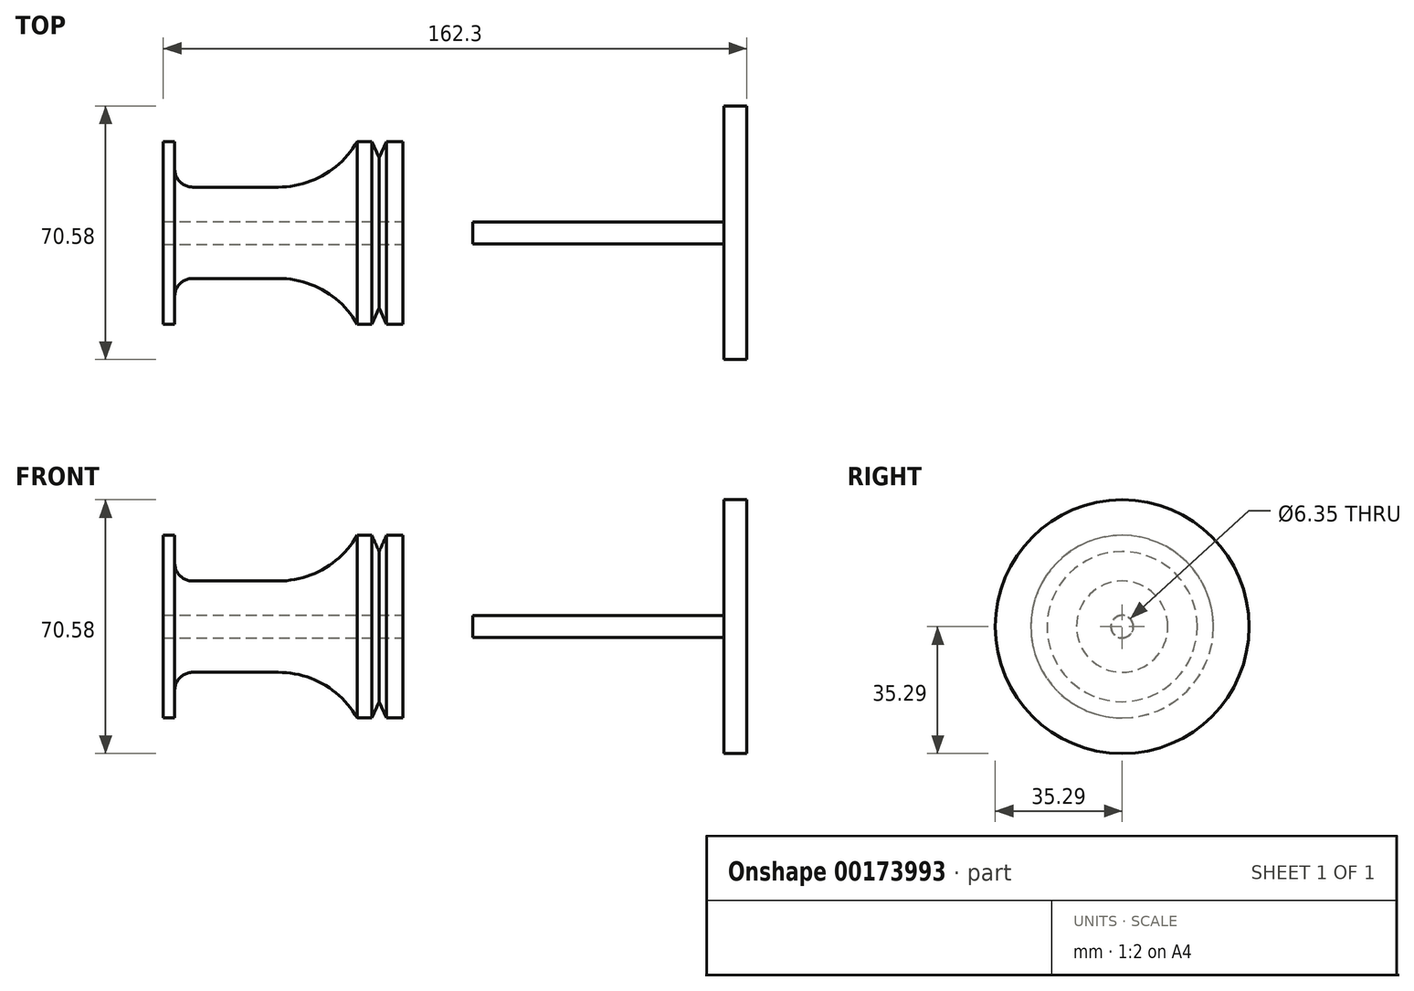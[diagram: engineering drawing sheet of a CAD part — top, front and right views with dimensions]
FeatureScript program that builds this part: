
annotation { "Feature Type Name" : "Feature", "Feature Type Description" : "" }
export const myFeature = defineFeature(function(context is Context, id is Id, definition is map)
    precondition{}
    {
        {
            var Q0;
            Q0=qCreatedBy(makeId("Front.planeOp"),FACE);
            var sketch = newSketch(context, id + "F0", { "sketchPlane" : qUnion([Q0])});
            skLineSegment(sketch, "E0", {"start": v(-70.82, 0) * mm, "end": v(-70.82, 25.4) * mm});
            skLineSegment(sketch, "E1", {"start": v(-70.82, 25.4) * mm, "end": v(-67.64, 25.4) * mm});
            skLineSegment(sketch, "E2", {"start": v(-67.64, 25.4) * mm, "end": v(-67.64, 12.7) * mm});
            skLineSegment(sketch, "E3", {"start": v(-67.64, 12.7) * mm, "end": v(-16.84, 12.7) * mm});
            skLineSegment(sketch, "E4", {"start": v(-16.84, 12.7) * mm, "end": v(-16.84, 25.4) * mm});
            skLineSegment(sketch, "E5", {"start": v(-16.84, 25.4) * mm, "end": v(-12.77, 25.4) * mm});
            skLineSegment(sketch, "E6", {"start": v(-4.14, 25.4) * mm, "end": v(-4.14, 0) * mm});
            skLineSegment(sketch, "E7", {"start": v(-4.14, 0) * mm, "end": v(-70.82, 0) * mm});
            skLineSegment(sketch, "E8", {"start": v(-79.36, 0) * mm, "end": v(74.16, 0) * mm, "construction": true});
            skLineSegment(sketch, "E9", {"start": v(-12.77, 25.4) * mm, "end": v(-10.76, 20.9) * mm});
            skLineSegment(sketch, "E10", {"start": v(-10.76, 20.9) * mm, "end": v(-8.75, 25.4) * mm});
            skLineSegment(sketch, "E11.trimOffspring", {"start": v(-8.75, 25.4) * mm, "end": v(-4.14, 25.4) * mm});
            skSolve(sketch);
        }
        {
            var Q0;
            Q0 = qSketchRegion(id + "F0", true);
            var Q1;
            Q1=sQuery(id+"F0.wireOp",EDGE,"E8");
            revolve(context, id + "F1", {"entities" : qUnion([Q0]), "axis" : qUnion([Q1]), "revolveType" : RevolveType.FULL});
        }
        {
            var Q0;
            Q0=makeQuery(id+"F1.opRevolve","SWEPT_EDGE",EDGE,{"disambiguationData":[OSD([sQuery(id+"F0.wireOp",EDGE,"E3"),sQuery(id+"F0.wireOp",EDGE,"E4")])]});
            fillet(context, id + "F2", {"entities" : qUnion([Q0]), "radius" : 25.4 * mm, "tangentPropagation" : true, "allowEdgeOverflow" : false});
        }
        {
            var Q0;
            Q0=makeQuery(id+"F1.opRevolve","SWEPT_FACE",FACE,{"disambiguationData":[OSD([sQuery(id+"F0.wireOp",EDGE,"E6")])]});
            var sketch = newSketch(context, id + "F3", { "sketchPlane" : qUnion([Q0])});
            skCircle(sketch, "E12", {"center": v(0, 0) * mm, "radius": 3.18 * mm});
            skSolve(sketch);
        }
        {
            var Q0;
            Q0 = qSketchRegion(id + "F3", true);
            extrude(context, id + "F4", {"entities" : qUnion([Q0]), "operationType" : NewBodyOperationType.REMOVE, "endBound" : BoundingType.THROUGH_ALL, "oppositeDirection" : true, "depth" : 25.4 * mm});
        }
        {
            var Q0;
            Q0=makeQuery(id+"F1.opRevolve","SWEPT_EDGE",EDGE,{"disambiguationData":[OSD([sQuery(id+"F0.wireOp",EDGE,"E2"),sQuery(id+"F0.wireOp",EDGE,"E3")])]});
            fillet(context, id + "F5", {"entities" : qUnion([Q0]), "radius" : 5.08 * mm, "tangentPropagation" : true, "allowEdgeOverflow" : false});
        }
        {
            var Q0;
            Q0=qCreatedBy(makeId("Front.planeOp"),FACE);
            var sketch = newSketch(context, id + "F6", { "sketchPlane" : qUnion([Q0])});
            skLineSegment(sketch, "E13", {"start": v(8, 0) * mm, "end": v(98.23, 0) * mm, "construction": true});
            skLineSegment(sketch, "E14", {"start": v(15.28, 0) * mm, "end": v(15.28, 3.05) * mm});
            skLineSegment(sketch, "E15", {"start": v(15.28, 3.05) * mm, "end": v(85.13, 3.05) * mm});
            skLineSegment(sketch, "E16", {"start": v(85.13, 3.05) * mm, "end": v(85.13, 35.29) * mm});
            skLineSegment(sketch, "E17", {"start": v(85.13, 35.29) * mm, "end": v(91.48, 35.29) * mm});
            skLineSegment(sketch, "E18", {"start": v(91.48, 35.29) * mm, "end": v(91.48, 0) * mm});
            skLineSegment(sketch, "E19", {"start": v(91.48, 0) * mm, "end": v(15.28, 0) * mm});
            skSolve(sketch);
        }
        {
            var Q0;
            Q0 = qSketchRegion(id + "F6", true);
            var Q1;
            Q1=sQuery(id+"F6.wireOp",EDGE,"E13");
            revolve(context, id + "F7", {"entities" : qUnion([Q0]), "axis" : qUnion([Q1]), "revolveType" : RevolveType.FULL});
        }
    });
